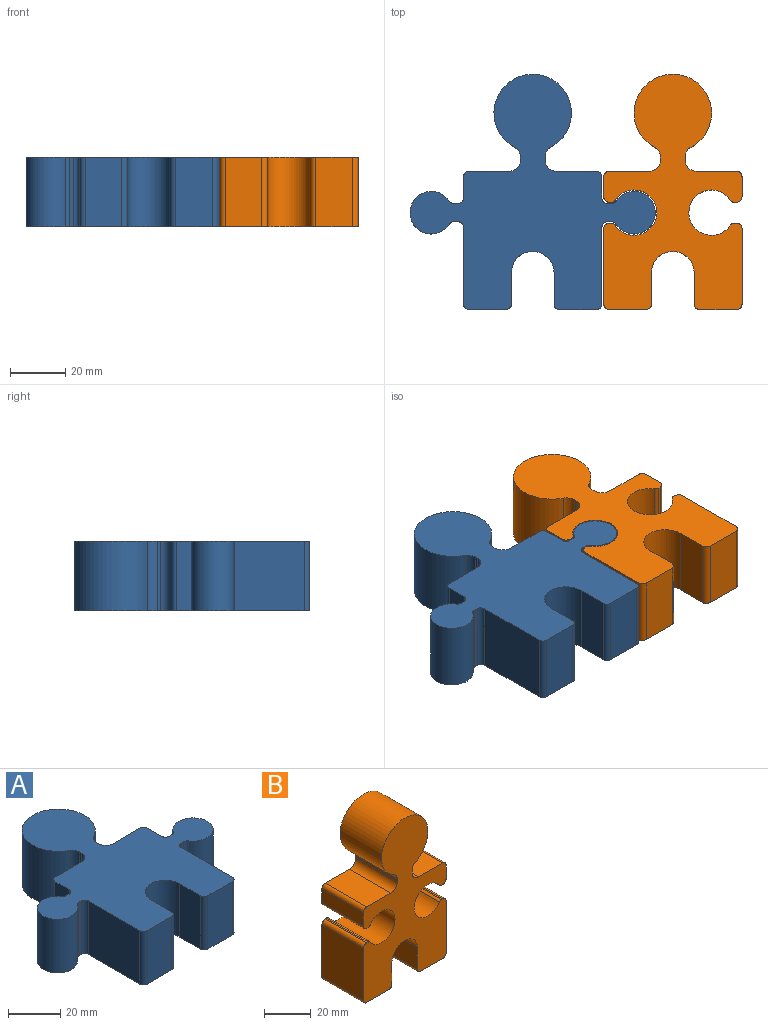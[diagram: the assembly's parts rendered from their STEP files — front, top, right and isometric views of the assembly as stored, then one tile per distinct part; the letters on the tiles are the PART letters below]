
ASSEMBLY  parts=2 mates=1
PART A: 40 faces, bbox 88.7x85x25 mm
  f0: cylinder r=2mm len=25mm, axis (0,0,-1), area 49.8mm2, adj f1,f37,f38,f39
  f1: cylinder r=7.7mm len=25mm, axis (0,0,-1), area 988.3mm2, adj f0,f2,f38,f39
  f2: cylinder r=2mm len=25mm, axis (0,0,-1), area 49.8mm2, adj f1,f3,f38,f39
  f3: plane 25x1.5mm, normal (0,-1,0), area 37.5mm2, adj f2,f4,f38,f39
  f4: cylinder r=2mm len=25mm, axis (0,0,-1), area 78.5mm2, adj f3,f5,f38,f39
  f5: plane 27.73x25mm, normal (-1,0,0), area 693.2mm2, adj f4,f6,f38,f39
  f6: cylinder r=2mm len=25mm, axis (0,0,-1), area 78.5mm2, adj f5,f7,f38,f39
  f7: plane 25x13.3mm, normal (0,-1,0), area 332.5mm2, adj f6,f8,f38,f39
  f8: cylinder r=2mm len=25mm, axis (0,0,-1), area 78.5mm2, adj f7,f9,f38,f39
  f9: plane 25x11.3mm, normal (1,0,0), area 282.5mm2, adj f8,f10,f38,f39
  f10: cylinder r=7.7mm len=25mm, axis (0,0,-1), area 604.8mm2, adj f9,f11,f38,f39
  f11: plane 25x11.3mm, normal (-1,0,0), area 282.5mm2, adj f10,f12,f38,f39
  f12: cylinder r=2mm len=25mm, axis (0,0,-1), area 78.5mm2, adj f11,f13,f38,f39
  f13: plane 25x13.3mm, normal (0,-1,0), area 332.5mm2, adj f12,f14,f38,f39
  f14: cylinder r=2mm len=25mm, axis (0,0,-1), area 78.5mm2, adj f13,f15,f38,f39
  f15: plane 27.73x25mm, normal (1,0,0), area 693.2mm2, adj f14,f16,f38,f39
  f16: cylinder r=2mm len=25mm, axis (0,0,-1), area 78.5mm2, adj f15,f17,f38,f39
  f17: plane 25x1.5mm, normal (0,-1,0), area 37.5mm2, adj f16,f18,f38,f39
  f18: cylinder r=2mm len=25mm, axis (0,0,-1), area 49.8mm2, adj f17,f19,f38,f39
  f19: cylinder r=7.7mm len=25mm, axis (0,0,-1), area 988.3mm2, adj f18,f20,f38,f39
  f20: cylinder r=2mm len=25mm, axis (0,0,-1), area 49.8mm2, adj f19,f21,f38,f39
  f21: plane 25x1.5mm, normal (0,1,0), area 37.5mm2, adj f20,f22,f38,f39
  f22: cylinder r=2mm len=25mm, axis (0,0,-1), area 78.5mm2, adj f21,f23,f38,f39
  f23: plane 25x7.73mm, normal (1,0,0), area 193.2mm2, adj f22,f24,f38,f39
  f24: cylinder r=2mm len=25mm, axis (0,0,-1), area 78.5mm2, adj f23,f25,f38,f39
  f25: plane 25x14.53mm, normal (0,1,0), area 363.2mm2, adj f24,f26,f38,f39
  f26: cylinder r=4mm len=25mm, axis (0,0,-1), area 157.1mm2, adj f25,f27,f38,f39
  f27: plane 25x1.12mm, normal (1,0,0), area 27.9mm2, adj f26,f28,f38,f39
  f28: cylinder r=4mm len=25mm, axis (0,0,-1), area 108.1mm2, adj f27,f29,f38,f39
  f29: cylinder r=14mm len=28mm, axis (0,0,-1), area 1856.1mm2, adj f28,f30,f38,f39
  f30: cylinder r=4mm len=25mm, axis (0,0,-1), area 108.1mm2, adj f29,f31,f38,f39
  f31: plane 25x1.12mm, normal (-1,0,0), area 27.9mm2, adj f30,f32,f38,f39
  f32: cylinder r=4mm len=25mm, axis (0,0,-1), area 157.1mm2, adj f31,f33,f38,f39
  f33: plane 25x14.53mm, normal (0,1,0), area 363.2mm2, adj f32,f34,f38,f39
  f34: cylinder r=2mm len=25mm, axis (0,0,-1), area 78.5mm2, adj f33,f35,f38,f39
  f35: plane 25x7.73mm, normal (-1,0,0), area 193.2mm2, adj f34,f36,f38,f39
  f36: cylinder r=2mm len=25mm, axis (0,0,-1), area 78.5mm2, adj f35,f37,f38,f39
  f37: plane 25x1.5mm, normal (0,1,0), area 37.5mm2, adj f0,f36,f38,f39
  f38: plane 88.69x85mm, normal (0,0,1), area 3318mm2, adj f0,f1,f2,f3,f4,f5,f6,f7
  f39: plane 88.69x85mm, normal (0,0,-1), area 3318mm2, adj f0,f1,f2,f3,f4,f5,f6,f7
PART B: 40 faces, bbox 50x25x85 mm
  f0: plane 25x0.86mm, normal (0,0,-1), area 21.4mm2, adj f1,f37,f38,f39
  f1: cylinder r=1.5mm len=25mm, axis (0,1,0), area 37.4mm2, adj f0,f2,f38,f39
  f2: cylinder r=8.2mm len=25mm, axis (0,1,0), area 1052.5mm2, adj f1,f3,f38,f39
  f3: cylinder r=1.5mm len=25mm, axis (0,1,0), area 37.4mm2, adj f2,f4,f38,f39
  f4: plane 25x0.86mm, normal (0,0,1), area 21.4mm2, adj f3,f5,f38,f39
  f5: cylinder r=2mm len=25mm, axis (0,1,0), area 78.5mm2, adj f4,f6,f38,f39
  f6: plane 27.23x25mm, normal (-1,0,0), area 680.7mm2, adj f5,f7,f38,f39
  f7: cylinder r=2mm len=25mm, axis (0,1,0), area 78.5mm2, adj f6,f8,f38,f39
  f8: plane 25x13.3mm, normal (0,0,-1), area 332.5mm2, adj f7,f9,f38,f39
  f9: cylinder r=2mm len=25mm, axis (0,1,0), area 78.5mm2, adj f8,f10,f38,f39
  f10: plane 25x11.3mm, normal (1,0,0), area 282.5mm2, adj f9,f11,f38,f39
  f11: cylinder r=7.7mm len=25mm, axis (0,1,0), area 604.8mm2, adj f10,f12,f38,f39
  f12: plane 25x11.3mm, normal (-1,0,0), area 282.5mm2, adj f11,f13,f38,f39
  f13: cylinder r=2mm len=25mm, axis (0,1,0), area 78.5mm2, adj f12,f14,f38,f39
  f14: plane 25x13.3mm, normal (0,0,-1), area 332.5mm2, adj f13,f15,f38,f39
  f15: cylinder r=2mm len=25mm, axis (0,1,0), area 78.5mm2, adj f14,f16,f38,f39
  f16: plane 27.23x25mm, normal (1,0,0), area 680.7mm2, adj f15,f17,f38,f39
  f17: cylinder r=2mm len=25mm, axis (0,1,0), area 78.5mm2, adj f16,f18,f38,f39
  f18: plane 25x0.86mm, normal (0,0,1), area 21.4mm2, adj f17,f19,f38,f39
  f19: cylinder r=1.5mm len=25mm, axis (0,1,0), area 37.4mm2, adj f18,f20,f38,f39
  f20: cylinder r=8.2mm len=25mm, axis (0,1,0), area 1052.5mm2, adj f19,f21,f38,f39
  f21: cylinder r=1.5mm len=25mm, axis (0,1,0), area 37.4mm2, adj f20,f22,f38,f39
  f22: plane 25x0.86mm, normal (0,0,-1), area 21.4mm2, adj f21,f23,f38,f39
  f23: cylinder r=2mm len=25mm, axis (0,1,0), area 78.5mm2, adj f22,f24,f38,f39
  f24: plane 25x7.23mm, normal (1,0,0), area 180.7mm2, adj f23,f25,f38,f39
  f25: cylinder r=2mm len=25mm, axis (0,1,0), area 78.5mm2, adj f24,f26,f38,f39
  f26: plane 25x14.53mm, normal (0,0,1), area 363.2mm2, adj f25,f27,f38,f39
  f27: cylinder r=4mm len=25mm, axis (0,1,0), area 157.1mm2, adj f26,f28,f38,f39
  f28: plane 25x1.12mm, normal (1,0,0), area 27.9mm2, adj f27,f29,f38,f39
  f29: cylinder r=4mm len=25mm, axis (0,1,0), area 108.1mm2, adj f28,f30,f38,f39
  f30: cylinder r=14mm len=28mm, axis (0,1,0), area 1856.1mm2, adj f29,f31,f38,f39
  f31: cylinder r=4mm len=25mm, axis (0,1,0), area 108.1mm2, adj f30,f32,f38,f39
  f32: plane 25x1.12mm, normal (-1,0,0), area 27.9mm2, adj f31,f33,f38,f39
  f33: cylinder r=4mm len=25mm, axis (0,1,0), area 157.1mm2, adj f32,f34,f38,f39
  f34: plane 25x14.53mm, normal (0,0,1), area 363.2mm2, adj f33,f35,f38,f39
  f35: cylinder r=2mm len=25mm, axis (0,1,0), area 78.5mm2, adj f34,f36,f38,f39
  f36: plane 25x7.23mm, normal (-1,0,0), area 180.7mm2, adj f35,f37,f38,f39
  f37: cylinder r=2mm len=25mm, axis (0,1,0), area 78.5mm2, adj f0,f36,f38,f39
  f38: plane 85x50mm, normal (0,-1,0), area 2413.4mm2, adj f0,f1,f2,f3,f4,f5,f6,f7
  f39: plane 85x50mm, normal (0,1,0), area 2413.4mm2, adj f0,f1,f2,f3,f4,f5,f6,f7
PLACE A t=(10.94,2.82,-14.53)mm
PLACE B rot(axis=(-1,0,0),90deg) t=(79.8,1.61,-14.53)mm
MATE fastened A.f19 <-> B.f2  axis (0,0,1) through (47.58,12.82,10.47)mm
